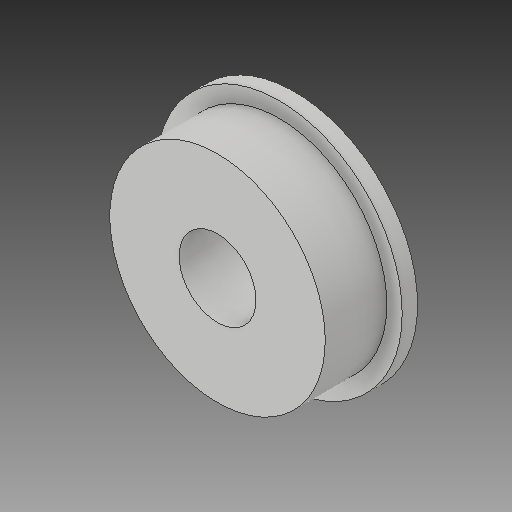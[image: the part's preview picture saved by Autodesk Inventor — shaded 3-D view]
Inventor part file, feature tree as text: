
AUTODESK INVENTOR PART (.ipt)
format: ipt  version: 2017 (Build 210142000, 142)  size: 129,024 bytes
history: native  units: mm
features: other x3, sketch x3
ambient origin geometry x8: Origin, YZ Plane, XZ Plane, XY Plane, X Axis, Y Axis, Z Axis, Center Point
bodies: Solid1 (feature_tree)
feature tree (6):
  other  "Flanged Bearing_CPY.ipt"
  other  "Solid1::Flanged Bearing_CPY.ipt"
  other  "TaggingFeature1"
  sketch  "Sketch1"  dims[d0=10.0mm]
  sketch  "Sketch2"
  sketch  "Sketch3"
